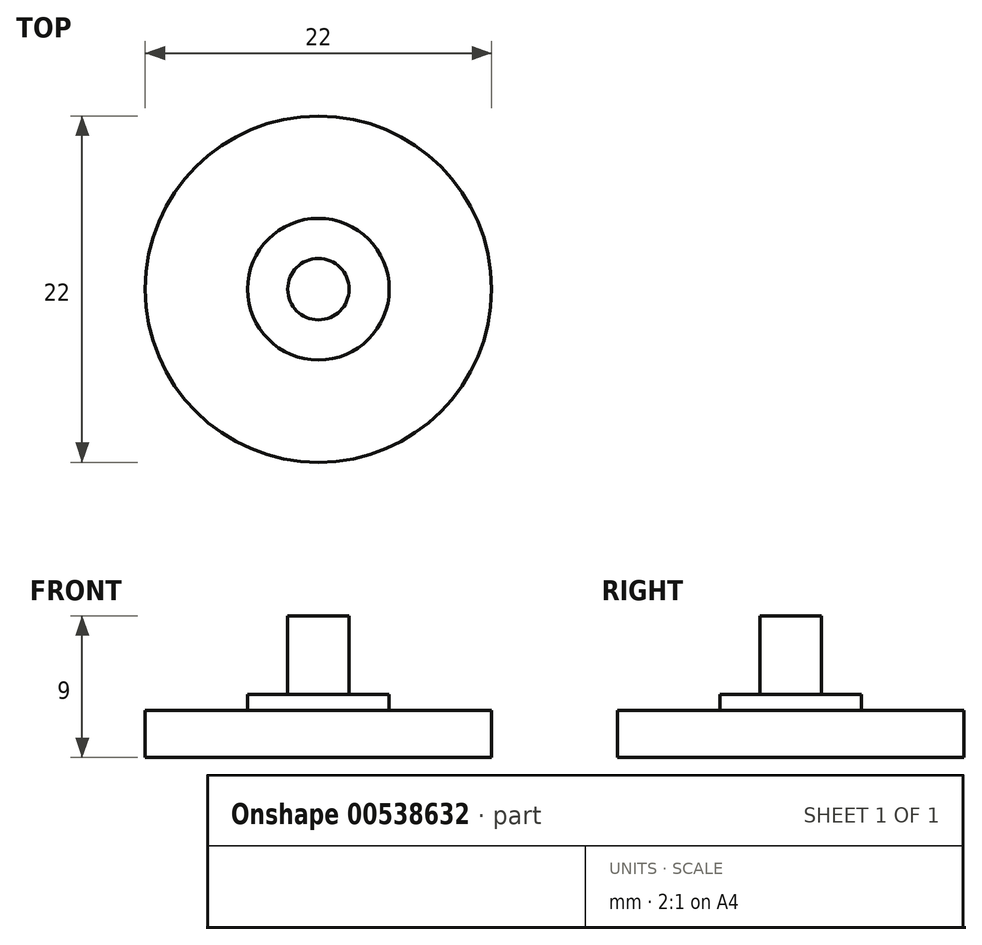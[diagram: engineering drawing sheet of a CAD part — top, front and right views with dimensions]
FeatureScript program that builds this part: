
annotation { "Feature Type Name" : "Feature", "Feature Type Description" : "" }
export const myFeature = defineFeature(function(context is Context, id is Id, definition is map)
    precondition{}
    {
        {
            var Q0;
            Q0=qCreatedBy(makeId("Top.planeOp"),FACE);
            var sketch = newSketch(context, id + "F0", { "sketchPlane" : qUnion([Q0])});
            skCircle(sketch, "E0", {"center": v(0, 0) * mm, "radius": 11 * mm});
            skSolve(sketch);
        }
        {
            var Q0;
            Q0=makeQuery(id+"F0.imprint","IMPRINT",FACE,{"disambiguationData":[TD([[makeQuery(id+"F0.imprint","IMPRINT",EDGE,{"derivedFrom":sQuery(id+"F0.wireOp",EDGE,"E0")}),1.0]])]});
            extrude(context, id + "F1", {"entities" : qUnion([Q0]), "depth" : 3 * mm, "offsetDistance" : 25 * mm});
        }
        {
            var Q0;
            Q0=makeQuery(id+"F1.opExtrude","CAP_FACE",FACE,{"disambiguationData":[OSD([sQuery(id+"F0.wireOp",EDGE,"E0")])],"isStart":false});
            var sketch = newSketch(context, id + "F2", { "sketchPlane" : qUnion([Q0])});
            skCircle(sketch, "E1", {"center": v(0, 0) * mm, "radius": 4.5 * mm});
            skSolve(sketch);
        }
        {
            var Q0;
            Q0=makeQuery(id+"F2.imprint","IMPRINT",FACE,{"disambiguationData":[TD([[makeQuery(id+"F2.imprint","IMPRINT",EDGE,{"derivedFrom":sQuery(id+"F2.wireOp",EDGE,"E1")}),1.0]])]});
            extrude(context, id + "F3", {"entities" : qUnion([Q0]), "operationType" : NewBodyOperationType.ADD, "depth" : 1 * mm, "offsetDistance" : 25 * mm});
        }
        {
            var Q0;
            Q0=makeQuery(id+"F3.opExtrude","CAP_FACE",FACE,{"disambiguationData":[OSD([sQuery(id+"F2.wireOp",EDGE,"E1")])],"isStart":false});
            var sketch = newSketch(context, id + "F4", { "sketchPlane" : qUnion([Q0])});
            skCircle(sketch, "E2", {"center": v(0, 0) * mm, "radius": 1.95 * mm});
            skSolve(sketch);
        }
        {
            var Q0;
            Q0=makeQuery(id+"F4.imprint","IMPRINT",FACE,{"disambiguationData":[TD([[makeQuery(id+"F4.imprint","IMPRINT",EDGE,{"derivedFrom":sQuery(id+"F4.wireOp",EDGE,"E2")}),1.0]])]});
            extrude(context, id + "F5", {"entities" : qUnion([Q0]), "operationType" : NewBodyOperationType.ADD, "depth" : 5 * mm, "offsetDistance" : 25 * mm});
        }
    });
